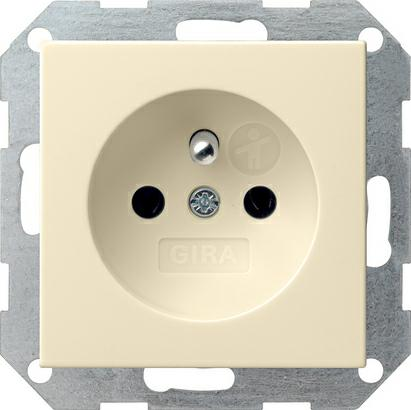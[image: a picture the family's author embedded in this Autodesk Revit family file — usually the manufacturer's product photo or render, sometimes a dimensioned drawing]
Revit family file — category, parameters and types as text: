
# Revit family: E_Cable Junction Box_MEPcontent_Spelsberg_IBTronic XL Drillbox 150_INT-EN
name_source: partatom
category: Electrical Fixtures
revit_build: Autodesk Revit 2017 (Build: 20160225_1515(x64)
units: mm (PartAtom-declared; Revit-internal decimal feet)

## family parameters
Always vertical = Yes
Cut with Voids When Loaded = No
Maintain Annotation Orientation = Yes
OmniClass Number = 23.80.30.14.24
OmniClass Title = Junction Boxes
Part Type = Junction Box
Room Calculation Point = No
Round Connector Dimension = Use Diameter
Shared = No
Work Plane-Based = No

## types (2) — shared parameters
3D Representation = 3DGeometry
ETIM Article Class = EC000414
Height = 92 mm  [stored 0.301837 ft]
IFCExportAs = IfcJunctionBox
IFCExportType = NOTDEFINED
Length = 280 mm  [stored 0.918635 ft]
Manufacturer = Spelsberg
Manufacturer URL = http://www.spelsberg.com
Product Line = Spelsberg
Revit Version = 2017
Rotation U-Axis Correction = 0.00°
Rotation U-Axis Default Correction = 0.00°
Rotation V-Axis Correction = 0.00°
Rotation V-Axis Default Correction = 0.00°
Rotation W-Axis Correction = 0.00°
Rotation W-Axis Default Correction = 0.00°
Voltage = 230 V
Width = 252 mm  [stored 0.826772 ft]

## per-type parameters (varying)
| type | Article Description | Conduit Diameter 1 | Conduit Diameter 2 | Description | Manufacturer Art. No. | Side Distance | Side Offset |
| IBTronic XL Drillbox 150 | Enclosure IBTronic XL Drillbox | 20 mm | 25 mm  [stored 0.082021 ft] | Enclosure IBTronic XL Drillbox | 97680401 | 11 mm | 2 mm  [stored 0.00656168 ft] |
| IBTronic XL Drillbox 150 E | Enclosure IBTronic XL Drillbox E | 16 mm  [stored 0.0524934 ft] | 19 mm  [stored 0.062336 ft] | Enclosure IBTronic XL Drillbox E | 97680402 | 12 mm  [stored 0.0393701 ft] | 6 mm  [stored 0.019685 ft] |

note: column(s) folded — value = type name in every type: Article Type, Model

note: [stored X ft] marks values corroborated as IEEE doubles in the binary element streams (Revit-internal decimal feet)

## geometry (parser evidence)
native form markers: Sweep x21
no freeform markers — native parametric forms only
